# Revit family: Drain_Floor-Jay R.Smith-Round_Type-1074X_Series
name_source: partatom
category: Plumbing Fixtures
units: mm (PartAtom-declared; Revit-internal decimal feet)

## family parameters
Always vertical = Yes
Cut with Voids When Loaded = No
OmniClass Number = 23.70.50.21.24
OmniClass Title = Waste Water Drains
Part Type = Normal
Room Calculation Point = No
Round Connector Dimension = Use Radius
Shared = No
Work Plane-Based = Yes

## types (21) — shared parameters
"L" Shaped Underdeck Clamp -CL = No
Aluminum Dome -AD = No
Assembly Code = D2030300
Bronze Standpipe -BZS = No
CW Connection = No
Cast Iron Dome -CID = No
Cast Iron Standpipe -CIS = No
Default Elevation = 0"
Description = Large General Pupose Roof Drain Adjustable Top with Standpipe
Diameter = 15 1/4"
Dome Material = Plastic-Jay R. Smith-Polyethene
E02, 2"(51) = No
E04, 4"(100) = No
E06, 6"(150) = No
Expansion Joint (Specify Fig. 1710) = No
Finish = Cast Iron-Jay R. Smith-Duco Coated
Galvanized Cast Iron Body & Collar -G = No
Galvanized Cast Iron Dome -CIDG = No
HW Connection = No
IAPMO Compliance = Meets ASME Standard A112.6.3-2001-02(50), 03(75) or 04"(100) sizes only
Installation Type = Floor Mounted
L - Speedi-Set Service Weight - 02"(50), 03"(75) & 04"(100) sizes only = No
LXH - Speedi-Set Extra Heavy - 02"(50), 03"(75) & 04"(100) sizes only = No
Manufacturer = Jay R. Smith
Material = Cast Iron-Jay R. Smith-Duco Coated
Product Page URL = https://www.jrsmith.com
Rough Bronze Dome -RBD = No
Secondary Flashing Clamp -C2 = No
Sump Receiver -R = No
T - Threaded Outlet = No
Trap Primer Connection Diameter = 1/2"
Trap Primer Connection Radius = 1/4"
URL = http://www.jrsmith.com
Underdeck Clamp -C = No
Vandal Proof Dome -U = No
Vent Connection = No
Waste Connection = Yes

## per-type parameters (varying)
| type | B | Connection Type | Outlet Diameter | Outlet Radius | Position Height (XX) | Strainer Diameter | Strainer Radius | Void Height |
| 1074Y02 | 4" | 2" No-HUB Outlet Connection | 2" | 1" | 1" | 4" | 2" | 3/4" |
| 1074Y03 | 4" | 3" No-HUB Outlet Connection | 3" | 1 1/2" | 0" | 3" | 1 1/2" | 1/4" |
| 1074Y04 | 4" | 4" No-HUB Outlet Connection | 4" | 2" | 0" | 3" | 1 1/2" | 1/4" |
| 1074Y05 | 6" | 5" No-HUB Outlet Connection | 5" | 2 1/2" | 0" | 3" | 1 1/2" | 1/4" |
| 1074Y06 | 6" | 6" No-HUB Outlet Connection | 6" | 3" | 1" | 3" | 1 1/2" | 1/4" |
| 1074L04 | 4" | 4" Speedi-Set Outlet Connection | 4" | 2" | 1" | 4" | 2" | 3/4" |
| 1074L03 | 4" | 3" Speedi-Set Outlet Connection | 3" | 1 1/2" | 2" | 4" | 2" | 3/4" |
| 1074L02 | 4" | 2" Speedi-Set Outlet Connection | 2" | 1" | 0" | 3" | 1 1/2" | 1/4" |
| 1074Y08 | 8" | 8" No-HUB Outlet Connection | 8" | 4" | 1" | 3" | 1 1/2" | 1/4" |
| 1074C02 | 4" | 2" Caulk Outlet Connection | 2" | 1" | 6" | 4" | 2" | 3/4" |
| 1074C03 | 4" | 3" Caulk Outlet Connection | 3" | 1 1/2" | 0" | 3" | 1 1/2" | 1/4" |
| 1074C04 | 4" | 4" Caulk Outlet Connection | 4" | 2" | 0" | 3" | 1 1/2" | 1/4" |
| 1074C05 | 6" | 5" Caulk Outlet Connection | 5" | 2 1/2" | 0" | 3" | 1 1/2" | 1/4" |
| 1074C06 | 6" | 6" Caulk Outlet Connection | 6" | 3" | 1" | 3" | 1 1/2" | 1/4" |
| 1074C08 | 8" | 8" Caulk Outlet Connection | 8" | 4" | 1" | 3" | 1 1/2" | 1/4" |
| 1074T02 | 4" | 2" Threaded Outlet Connection | 2" | 1" | 6" | 4" | 2" | 3/4" |
| 1074T03 | 4" | 3" Threaded Outlet Connection | 3" | 1 1/2" | 0" | 3" | 1 1/2" | 1/4" |
| 1074T04 | 4" | 4" Threaded Outlet Connection | 4" | 2" | 0" | 3" | 1 1/2" | 1/4" |
| 1074T05 | 6" | 5" Threaded Outlet Connection | 5" | 2 1/2" | 0" | 3" | 1 1/2" | 1/4" |
| 1074T06 | 6" | 6" Threaded Outlet Connection | 6" | 3" | 1" | 3" | 1 1/2" | 1/4" |
| 1074T08 | 8" | 8" Threaded Outlet Connection | 8" | 4" | 6" | 3" | 1 1/2" | 1/4" |

note: column(s) folded — value = type name in every type: Model

## geometry (parser evidence)
native form markers: Sweep x6
no freeform markers — native parametric forms only
